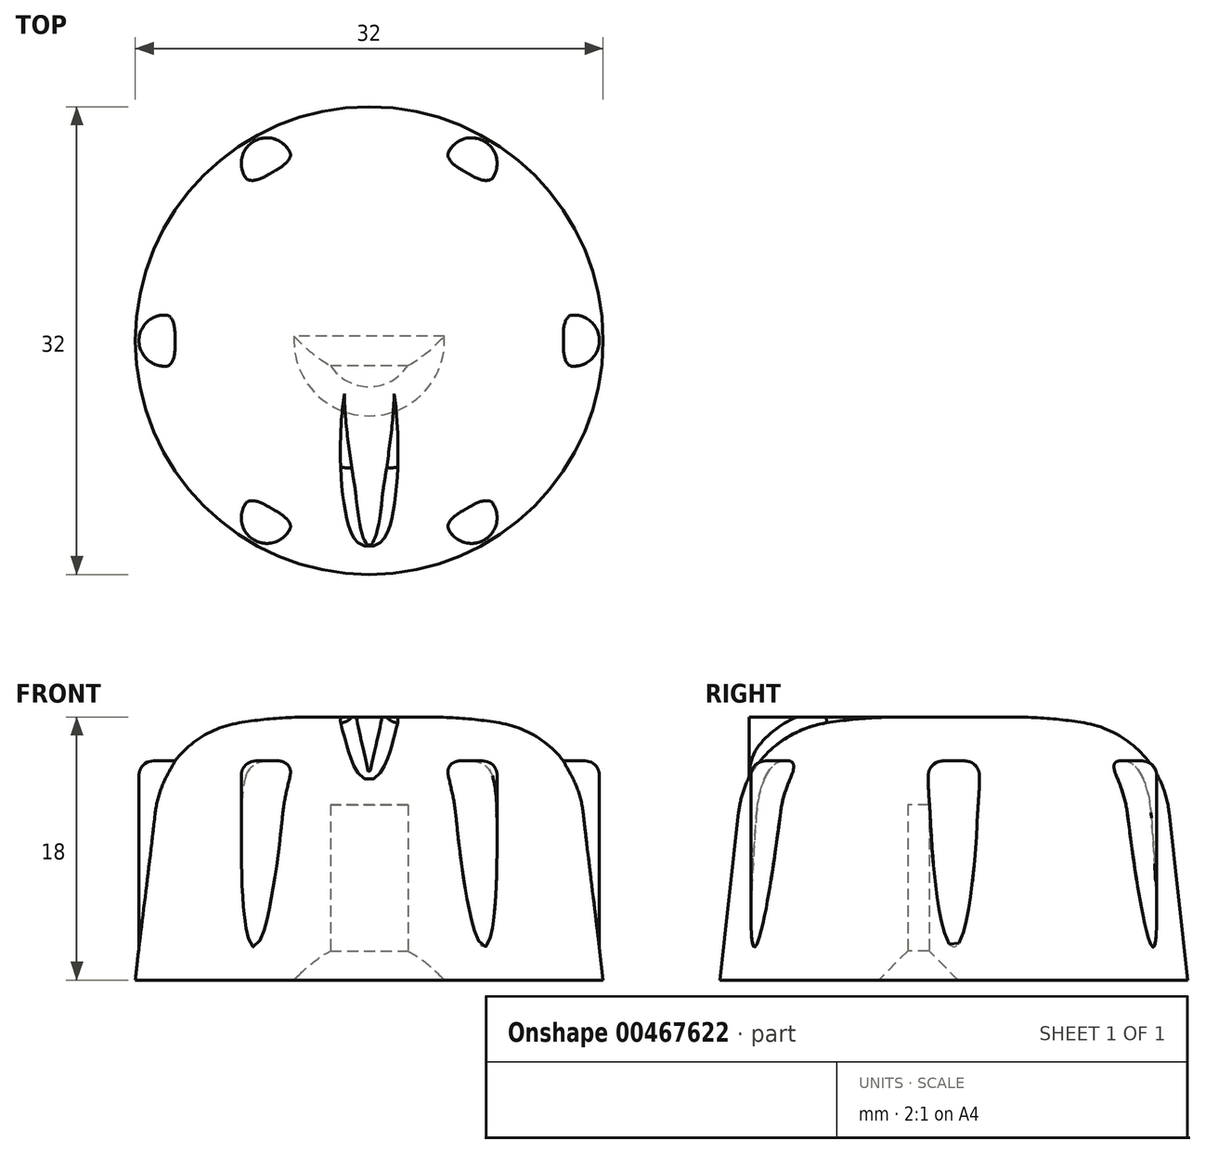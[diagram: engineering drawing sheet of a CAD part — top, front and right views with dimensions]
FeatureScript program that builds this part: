
annotation { "Feature Type Name" : "Feature", "Feature Type Description" : "" }
export const myFeature = defineFeature(function(context is Context, id is Id, definition is map)
    precondition{}
    {
        {
            var Q0;
            Q0=qCreatedBy(makeId("Front.planeOp"),FACE);
            var sketch = newSketch(context, id + "F0", { "sketchPlane" : qUnion([Q0])});
            skLineSegment(sketch, "E0", {"start": v(0, 18) * mm, "end": v(-14, 18) * mm});
            skLineSegment(sketch, "E1", {"start": v(-14, 18) * mm, "end": v(-16, 0) * mm});
            skLineSegment(sketch, "E2", {"start": v(-3.15, 0) * mm, "end": v(-3.15, 12) * mm});
            skLineSegment(sketch, "E3", {"start": v(-3.15, 12) * mm, "end": v(0, 12) * mm});
            skLineSegment(sketch, "E4", {"start": v(0, 12) * mm, "end": v(0, 18) * mm});
            skLineSegment(sketch, "E5", {"start": v(-16, 0) * mm, "end": v(-3.03, 0) * mm});
            skSolve(sketch);
        }
        {
            var Q0;
            Q0=makeQuery(id+"F0.imprint","IMPRINT",FACE,{"disambiguationData":[TD([[makeQuery(id+"F0.imprint","IMPRINT",EDGE,{"derivedFrom":sQuery(id+"F0.wireOp",EDGE,"E0")}),1.0]])]});
            var Q1;
            Q1=sQuery(id+"F0.wireOp",EDGE,"E4");
            revolve(context, id + "F1", {"entities" : qUnion([Q0]), "axis" : qUnion([Q1]), "revolveType" : RevolveType.FULL});
        }
        {
            var Q0;
            Q0=makeQuery(id+"F1.opRevolve","SWEPT_FACE",FACE,{"disambiguationData":[OSD([sQuery(id+"F0.wireOp",EDGE,"E5")])]});
            var sketch = newSketch(context, id + "F2", { "sketchPlane" : qUnion([Q0])});
            skCircle(sketch, "E6", {"center": v(0, 0) * mm, "radius": 3.15 * mm});
            skLineSegment(sketch, "E7", {"start": v(-3.77, 1.7) * mm, "end": v(4.4, 1.7) * mm});
            skSolve(sketch);
        }
        {
            var Q0;
            {var subQ0=sQuery(id+"F2.wireOp",EDGE,"E7");var subQ1=sQuery(id+"F2.wireOp",EDGE,"E6");var subQ2=makeQuery(id+"F2.imprint","INTERSECT",VERTEX,{"disambiguationData":[OD(0.0)],"derivedFrom":[subQ1,subQ0]});Q0=makeQuery(id+"F2.imprint","IMPRINT",FACE,{"disambiguationData":[TD([[makeQuery(id+"F2.imprint","IMPRINT",EDGE,{"disambiguationData":[TD([[subQ2,1.0]])],"derivedFrom":subQ1}),1.0]])]});}
            extrude(context, id + "F3", {"entities" : qUnion([Q0]), "operationType" : NewBodyOperationType.ADD, "oppositeDirection" : true, "depth" : 12 * mm});
        }
        {
            var Q0;
            Q0=makeQuery(id+"F1.opRevolve","SWEPT_EDGE",EDGE,{"disambiguationData":[OSD([sQuery(id+"F0.wireOp",EDGE,"E0"),sQuery(id+"F0.wireOp",EDGE,"E1")])]});
            chamfer(context, id + "F4", {"entities" : qUnion([Q0]), "width" : 2 * mm, "tangentPropagation" : true});
        }
        {
            var Q0;
            {var subQ0=sQuery(id+"F0.wireOp",EDGE,"E0");Q0=makeQuery(id+"F4.opChamfer","BLEND_EDGE",EDGE,{"blendedFrom":[makeQuery(id+"F1.opRevolve","SWEPT_EDGE",EDGE,{"disambiguationData":[OSD([subQ0,sQuery(id+"F0.wireOp",EDGE,"E1")])]}),makeQuery(id+"F1.opRevolve","SWEPT_FACE",FACE,{"disambiguationData":[OSD([subQ0])]})],"blendedInto":[makeQuery(id+"F1.opRevolve","SWEPT_FACE",FACE,{"disambiguationData":[OSD([subQ0])]})]});}
            fillet(context, id + "F5", {"entities" : qUnion([Q0]), "radius" : 30 * mm, "tangentPropagation" : true, "allowEdgeOverflow" : false});
        }
        {
            var Q0;
            {var subQ0=sQuery(id+"F0.wireOp",EDGE,"E1");var subQ1=sQuery(id+"F0.wireOp",EDGE,"E0");Q0=makeQuery(id+"F5.opFillet","BLEND_EDGE",EDGE,{"blendedFrom":[makeQuery(id+"F4.opChamfer","BLEND_EDGE",EDGE,{"blendedFrom":[makeQuery(id+"F1.opRevolve","SWEPT_EDGE",EDGE,{"disambiguationData":[OSD([subQ1,subQ0])]}),makeQuery(id+"F1.opRevolve","SWEPT_FACE",FACE,{"disambiguationData":[OSD([subQ1])]})],"blendedInto":[makeQuery(id+"F1.opRevolve","SWEPT_FACE",FACE,{"disambiguationData":[OSD([subQ1])]})]}),makeQuery(id+"F1.opRevolve","SWEPT_FACE",FACE,{"disambiguationData":[OSD([subQ0])]})],"blendedInto":[makeQuery(id+"F1.opRevolve","SWEPT_FACE",FACE,{"disambiguationData":[OSD([subQ0])]})]});}
            fillet(context, id + "F6", {"entities" : qUnion([Q0]), "radius" : 7 * mm, "tangentPropagation" : true, "allowEdgeOverflow" : false});
        }
        {
            var Q0;
            Q0=makeQuery(id+"F1.opRevolve","SWEPT_FACE",FACE,{"disambiguationData":[OSD([sQuery(id+"F0.wireOp",EDGE,"E0")])]});
            var sketch = newSketch(context, id + "F7", { "sketchPlane" : qUnion([Q0])});
            skEllipse(sketch, "E8", {"center": v(0, -8) * mm, "majorRadius": 6 * mm, "minorRadius": 1 * mm, "majorAxis": v(0, 1)});
            skSolve(sketch);
        }
        {
            var Q0;
            {var subQ0=sQuery(id+"F7.wireOp",EDGE,"E8");var subQ1=sQuery(id+"F0.wireOp",EDGE,"E0");var subQ2=makeQuery(id+"F1.opRevolve","SWEPT_FACE",FACE,{"disambiguationData":[OSD([subQ1])]});var subQ3=makeQuery(id+"F5.opFillet","BLEND_EDGE",EDGE,{"blendedFrom":[makeQuery(id+"F4.opChamfer","BLEND_EDGE",EDGE,{"blendedFrom":[makeQuery(id+"F1.opRevolve","SWEPT_EDGE",EDGE,{"disambiguationData":[OSD([subQ1,sQuery(id+"F0.wireOp",EDGE,"E1")])]}),subQ2],"blendedInto":[subQ2]}),subQ2],"blendedInto":[subQ2]});var subQ4=makeQuery(id+"F7.imprint","INTERSECT",VERTEX,{"disambiguationData":[OD(0.0)],"derivedFrom":[subQ3,subQ0]});Q0=makeQuery(id+"F7.imprint","IMPRINT",FACE,{"disambiguationData":[TD([[makeQuery(id+"F7.imprint","IMPRINT",EDGE,{"disambiguationData":[TD([[subQ4,-1.0]])],"derivedFrom":subQ0}),1.0]])]});}
            extrude(context, id + "F8", {"entities" : qUnion([Q0]), "operationType" : NewBodyOperationType.ADD, "oppositeDirection" : true, "depth" : 5 * mm});
        }
        {
            var Q0;
            Q0=makeQuery(id+"F8.boolean.opBoolean","INTERSECT",EDGE,{"disambiguationData":[OD(0.0)],"derivedFrom":[makeQuery(id+"F5.opFillet","BLEND_FACE",FACE,{"disambiguationData":[OSD([sQuery(id+"F0.wireOp",EDGE,"E0"),sQuery(id+"F0.wireOp",EDGE,"E1")])]}),makeQuery(id+"F8.opExtrude","SWEPT_FACE",FACE,{"disambiguationData":[OSD([sQuery(id+"F7.wireOp",EDGE,"E8")])]})]});
            var Q1;
            Q1=makeQuery(id+"F8.boolean.opBoolean","INTERSECT",EDGE,{"derivedFrom":[makeQuery(id+"F6.opFillet","BLEND_FACE",FACE,{"disambiguationData":[OSD([sQuery(id+"F0.wireOp",EDGE,"E0"),sQuery(id+"F0.wireOp",EDGE,"E1")])]}),makeQuery(id+"F8.opExtrude","SWEPT_FACE",FACE,{"disambiguationData":[OSD([sQuery(id+"F7.wireOp",EDGE,"E8")])]})]});
            var Q2;
            Q2=makeQuery(id+"F8.boolean.opBoolean","INTERSECT",EDGE,{"disambiguationData":[OD(1.0)],"derivedFrom":[makeQuery(id+"F5.opFillet","BLEND_FACE",FACE,{"disambiguationData":[OSD([sQuery(id+"F0.wireOp",EDGE,"E0"),sQuery(id+"F0.wireOp",EDGE,"E1")])]}),makeQuery(id+"F8.opExtrude","SWEPT_FACE",FACE,{"disambiguationData":[OSD([sQuery(id+"F7.wireOp",EDGE,"E8")])]})]});
            fillet(context, id + "F9", {"entities" : qUnion([Q0, Q1, Q2]), "radius" : 1 * mm, "tangentPropagation" : true, "allowEdgeOverflow" : false});
        }
        {
            var Q0;
            Q0=qCreatedBy(makeId("Top.planeOp"),FACE);
            var sketch = newSketch(context, id + "F10", { "sketchPlane" : qUnion([Q0])});
            skCircle(sketch, "E9", {"center": v(-14, 0) * mm, "radius": 1.75 * mm});
            skCircle(sketch, "E10.1.0", {"center": v(-7, -12.12) * mm, "radius": 1.75 * mm});
            skCircle(sketch, "E10.2.0", {"center": v(7, -12.12) * mm, "radius": 1.75 * mm});
            skCircle(sketch, "E10.3.0", {"center": v(14, 0) * mm, "radius": 1.75 * mm});
            skCircle(sketch, "E10.4.0", {"center": v(7, 12.12) * mm, "radius": 1.75 * mm});
            skCircle(sketch, "E10.5.0", {"center": v(-7, 12.12) * mm, "radius": 1.75 * mm});
            skPoint(sketch, "E10.center", {"position": v(0, 0) * mm});
            skSolve(sketch);
        }
        {
            var Q0;
            Q0=makeQuery(id+"F10.imprint","IMPRINT",FACE,{"disambiguationData":[TD([[makeQuery(id+"F10.imprint","IMPRINT",EDGE,{"derivedFrom":sQuery(id+"F10.wireOp",EDGE,"E9")}),1.0]])]});
            var Q1;
            Q1=makeQuery(id+"F10.imprint","IMPRINT",FACE,{"disambiguationData":[TD([[makeQuery(id+"F10.imprint","IMPRINT",EDGE,{"derivedFrom":sQuery(id+"F10.wireOp",EDGE,"E10.1.0")}),1.0]])]});
            var Q2;
            Q2=makeQuery(id+"F10.imprint","IMPRINT",FACE,{"disambiguationData":[TD([[makeQuery(id+"F10.imprint","IMPRINT",EDGE,{"derivedFrom":sQuery(id+"F10.wireOp",EDGE,"E10.2.0")}),1.0]])]});
            var Q3;
            Q3=makeQuery(id+"F10.imprint","IMPRINT",FACE,{"disambiguationData":[TD([[makeQuery(id+"F10.imprint","IMPRINT",EDGE,{"derivedFrom":sQuery(id+"F10.wireOp",EDGE,"E10.3.0")}),1.0]])]});
            var Q4;
            Q4=makeQuery(id+"F10.imprint","IMPRINT",FACE,{"disambiguationData":[TD([[makeQuery(id+"F10.imprint","IMPRINT",EDGE,{"derivedFrom":sQuery(id+"F10.wireOp",EDGE,"E10.4.0")}),1.0]])]});
            var Q5;
            Q5=makeQuery(id+"F10.imprint","IMPRINT",FACE,{"disambiguationData":[TD([[makeQuery(id+"F10.imprint","IMPRINT",EDGE,{"derivedFrom":sQuery(id+"F10.wireOp",EDGE,"E10.5.0")}),1.0]])]});
            extrude(context, id + "F11", {"entities" : qUnion([Q0, Q1, Q2, Q3, Q4, Q5]), "operationType" : NewBodyOperationType.ADD, "depth" : 15 * mm});
        }
        {
            var Q0;
            Q0=makeQuery(id+"F11.opExtrude","CAP_EDGE",EDGE,{"disambiguationData":[OSD([sQuery(id+"F10.wireOp",EDGE,"E10.4.0")])],"isStart":false});
            var Q1;
            Q1=makeQuery(id+"F11.opExtrude","CAP_EDGE",EDGE,{"disambiguationData":[OSD([sQuery(id+"F10.wireOp",EDGE,"E10.5.0")])],"isStart":false});
            var Q2;
            Q2=makeQuery(id+"F11.opExtrude","CAP_EDGE",EDGE,{"disambiguationData":[OSD([sQuery(id+"F10.wireOp",EDGE,"E9")])],"isStart":false});
            var Q3;
            Q3=makeQuery(id+"F11.opExtrude","CAP_EDGE",EDGE,{"disambiguationData":[OSD([sQuery(id+"F10.wireOp",EDGE,"E10.1.0")])],"isStart":false});
            var Q4;
            Q4=makeQuery(id+"F11.opExtrude","CAP_EDGE",EDGE,{"disambiguationData":[OSD([sQuery(id+"F10.wireOp",EDGE,"E10.2.0")])],"isStart":false});
            var Q5;
            Q5=makeQuery(id+"F11.opExtrude","CAP_EDGE",EDGE,{"disambiguationData":[OSD([sQuery(id+"F10.wireOp",EDGE,"E10.3.0")])],"isStart":false});
            fillet(context, id + "F12", {"entities" : qUnion([Q0, Q1, Q2, Q3, Q4, Q5]), "radius" : 1 * mm, "tangentPropagation" : true, "allowEdgeOverflow" : false});
        }
        {
            var Q0;
            Q0=makeQuery(id+"F3.opExtrude","CAP_EDGE",EDGE,{"disambiguationData":[OSD([sQuery(id+"F2.wireOp",EDGE,"E7")])],"isStart":true});
            var Q1;
            Q1=makeQuery(id+"F1.opRevolve","SWEPT_EDGE",EDGE,{"disambiguationData":[OSD([sQuery(id+"F0.wireOp",EDGE,"E2"),sQuery(id+"F0.wireOp",EDGE,"E5")])]});
            chamfer(context, id + "F13", {"entities" : qUnion([Q0, Q1]), "width" : 2 * mm});
        }
    });
